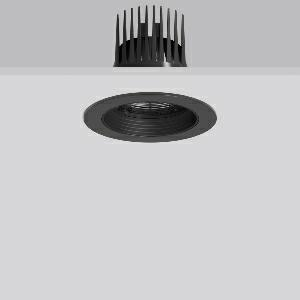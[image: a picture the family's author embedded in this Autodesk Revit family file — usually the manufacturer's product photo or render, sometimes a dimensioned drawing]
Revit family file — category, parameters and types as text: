
# Revit family: heledon_maxi_e_901762_003_3_76_1afa
name_source: partatom
category: Lighting Fixtures
units: mm (PartAtom-declared; Revit-internal decimal feet)

## family parameters
Cut with Voids When Loaded = No
Host = Face
Light Source = No
Part Type = Normal
Room Calculation Point = No
Round Connector Dimension = Use Diameter
Shared = No

## types (1)
- HELEDON maxi E (1 x LED Modul 935, 2850 lm, 3500)
    Apparent Load = 25 VA
    Approval mark = CE
    CIE Flux Codes = 96 100 100 100 100
    Color Rendering = 92
    Color Temperature = 3500
    Default Elevation = 1800 mm
    Description = Series: HELEDON maxi
Round recessed downlight. Housing: die-cast aluminium, powder-coated. Black plastic ring and recessed LED to prevent glare from the side. Optical assembly with lens made of plastic (polycarbonate) for the best homogeneous light distribution - can be changed without tools. Best colour rendering index Ra>90. Suitable for Recessed ceiling mounting. Installation without tools thanks to spring fastening system. Including separate LED converter with connecting cable 600 mm.High quality converter without flickering and stroboscopic effect. Through-wiring box (5 pole) available as accessory. The following accessories can be mounted without use of tools: interchangeable lenses, decorative glasses, honeycomb louvre, clear and frosted diffusers, white interchangeable plastic ring. 
Colour: deep black, matt (RAL 9005)
Diameter: 162 mm
Height: 3 mm
Cut-out diameter: 152 mm
Recess height: 200 mm
Luminaire: recess height: 135 mm
Lamp: LED
Socket: without socket
Colour temperature: 3500K
Colour rendering index (CRI): 92
System power: 25 W
Rated luminous flux: 2850 lm
Luminous efficiency: 114 lm/W
Control gear: Converter, dimmable, DALI
Protection class: II
Type of protection: IP 20
    Height = 0 mm  [stored 0 ft]
    Lamp = 1 x LED Modul 935
    Lamp Light Flux = 2850 lm
    Lamp count = 1
    Length = 162 mm
    Lifetime = 50000 h
    Luminous efficacy = 114 lm/W
    Manufacturer = RZB
    ModVariant = No
    Model = 901762.003.3.76
    Mounting Place = Ceiling
    Mounting Type = Recessed
    Number of Poles = 1
    OnlyDefault = Yes
    Power Factor = 1
    Product Name = HELEDON maxi E
    Product group = Recessed downlights
    ProductGroupID = 402
    Protection Class = Protection class II
    Protection Degree = IP 20
    RLX_Detail_Level = 1
    RLX_Emergency_Light_Flux = 0 lm
    RLX_Emergency_Type = 0
    RLX_Emergency_Type_DB = No
    RlxData = <blob elided: 122357 chars, md5=3b5acba8>
    Socket = socket
    Standby Power = 0 W
    System Light Flux = 2850 lm
    System Power = 25 W
    Type Comments = Product without accessories
    Type Image = 901663.003.jpg
    URL = http://relux.com
    VarID = ---
    Voltage = 230 V
    Voltage Range = 220-240 V
    Weight = 0.00 kg
    Width = 0 mm  [stored 0 ft]

note: [stored X ft] marks values corroborated as IEEE doubles in the binary element streams (Revit-internal decimal feet)

## geometry (parser evidence)
native form markers: Blend x4, Sweep x10
no freeform markers — native parametric forms only
